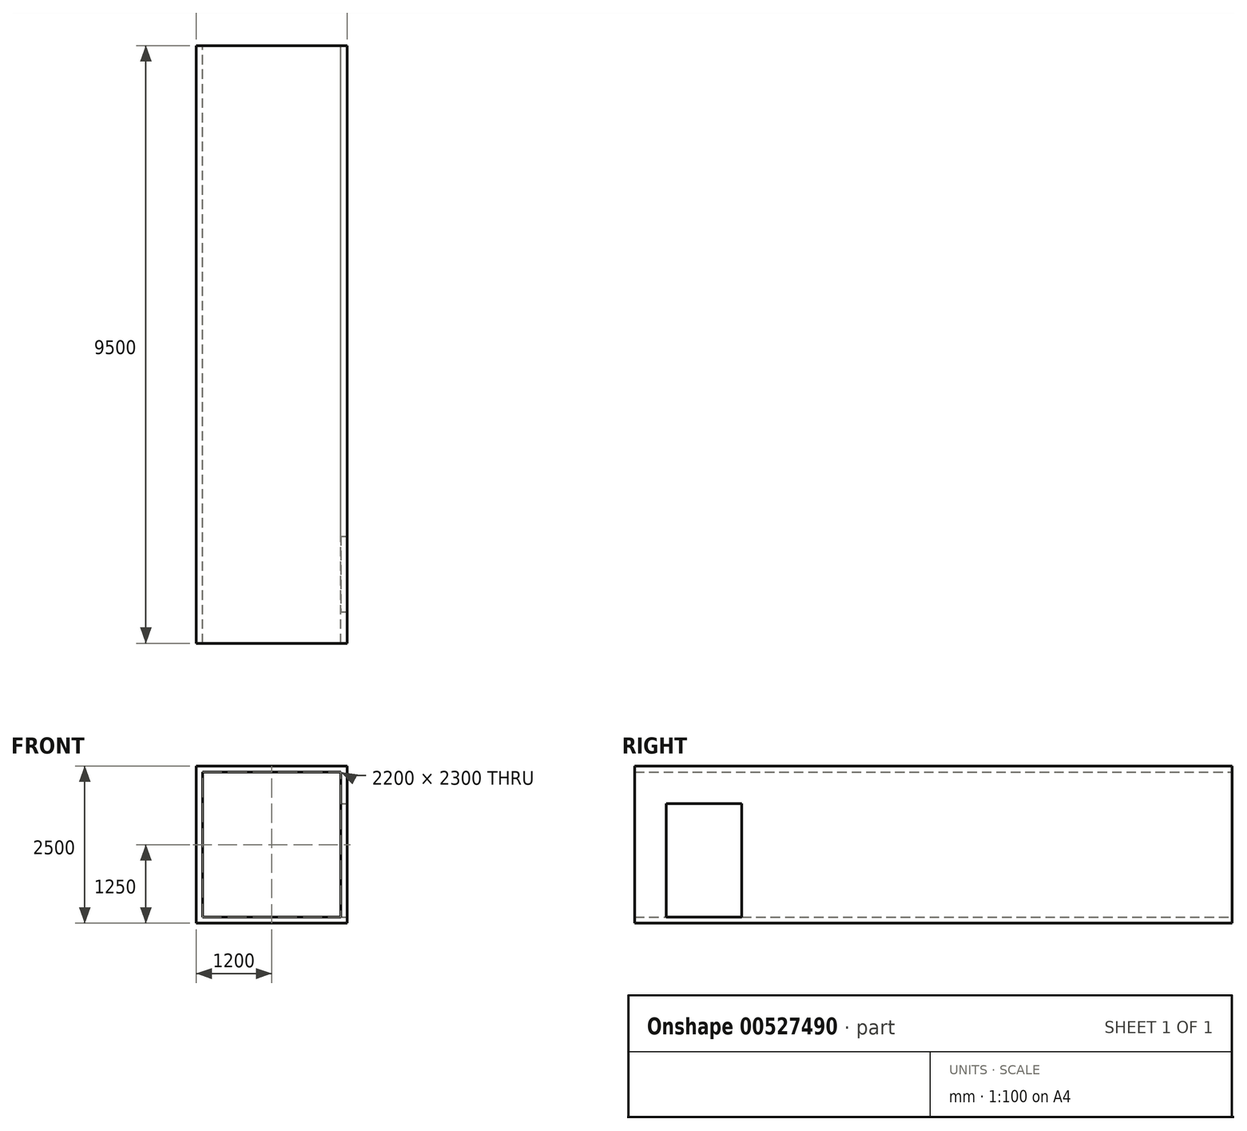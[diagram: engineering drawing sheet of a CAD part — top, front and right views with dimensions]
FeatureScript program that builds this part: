
annotation { "Feature Type Name" : "Feature", "Feature Type Description" : "" }
export const myFeature = defineFeature(function(context is Context, id is Id, definition is map)
    precondition{}
    {
        {
            var Q0;
            Q0=qCreatedBy(makeId("Front.planeOp"),FACE);
            var sketch = newSketch(context, id + "F0", { "sketchPlane" : qUnion([Q0])});
            skLineSegment(sketch, "E0.bottom", {"start": v(-1207.21, 1921.65) * mm, "end": v(1192.79, 1921.65) * mm});
            skLineSegment(sketch, "E0.top", {"start": v(-1207.21, -578.35) * mm, "end": v(1192.79, -578.35) * mm});
            skLineSegment(sketch, "E0.left", {"start": v(-1207.21, 1921.65) * mm, "end": v(-1207.21, -578.35) * mm});
            skLineSegment(sketch, "E0.right", {"start": v(1192.79, 1921.65) * mm, "end": v(1192.79, -578.35) * mm});
            skLineSegment(sketch, "E1.bottom", {"start": v(1092.79, 1821.65) * mm, "end": v(-1107.21, 1821.65) * mm});
            skLineSegment(sketch, "E1.top", {"start": v(1092.79, -478.35) * mm, "end": v(-1107.21, -478.35) * mm});
            skLineSegment(sketch, "E1.left", {"start": v(1092.79, 1821.65) * mm, "end": v(1092.79, -478.35) * mm});
            skLineSegment(sketch, "E1.right", {"start": v(-1107.21, 1821.65) * mm, "end": v(-1107.21, -478.35) * mm});
            skSolve(sketch);
        }
        {
            var Q0;
            Q0=makeQuery(id+"F0.imprint","IMPRINT",FACE,{"disambiguationData":[TD([[makeQuery(id+"F0.imprint","IMPRINT",EDGE,{"derivedFrom":sQuery(id+"F0.wireOp",EDGE,"E0.bottom")}),-1.0]])]});
            extrude(context, id + "F1", {"entities" : qUnion([Q0]), "depth" : 9500 * mm, "offsetDistance" : 25 * mm});
        }
        {
            var Q0;
            Q0=makeQuery(id+"F1.opExtrude","SWEPT_FACE",FACE,{"disambiguationData":[OSD([sQuery(id+"F0.wireOp",EDGE,"E0.right")])]});
            var sketch = newSketch(context, id + "F2", { "sketchPlane" : qUnion([Q0])});
            skLineSegment(sketch, "E2.bottom", {"start": v(-7800, 1321.65) * mm, "end": v(-9000, 1321.65) * mm});
            skLineSegment(sketch, "E2.top", {"start": v(-7800, -478.35) * mm, "end": v(-9000, -478.35) * mm});
            skLineSegment(sketch, "E2.left", {"start": v(-7800, 1321.65) * mm, "end": v(-7800, -478.35) * mm});
            skLineSegment(sketch, "E2.right", {"start": v(-9000, 1321.65) * mm, "end": v(-9000, -478.35) * mm});
            skSolve(sketch);
        }
        {
            var Q0;
            Q0 = qSketchRegion(id + "F2", true);
            extrude(context, id + "F3", {"entities" : qUnion([Q0]), "operationType" : NewBodyOperationType.REMOVE, "oppositeDirection" : true, "depth" : 100 * mm, "offsetDistance" : 25 * mm});
        }
    });
